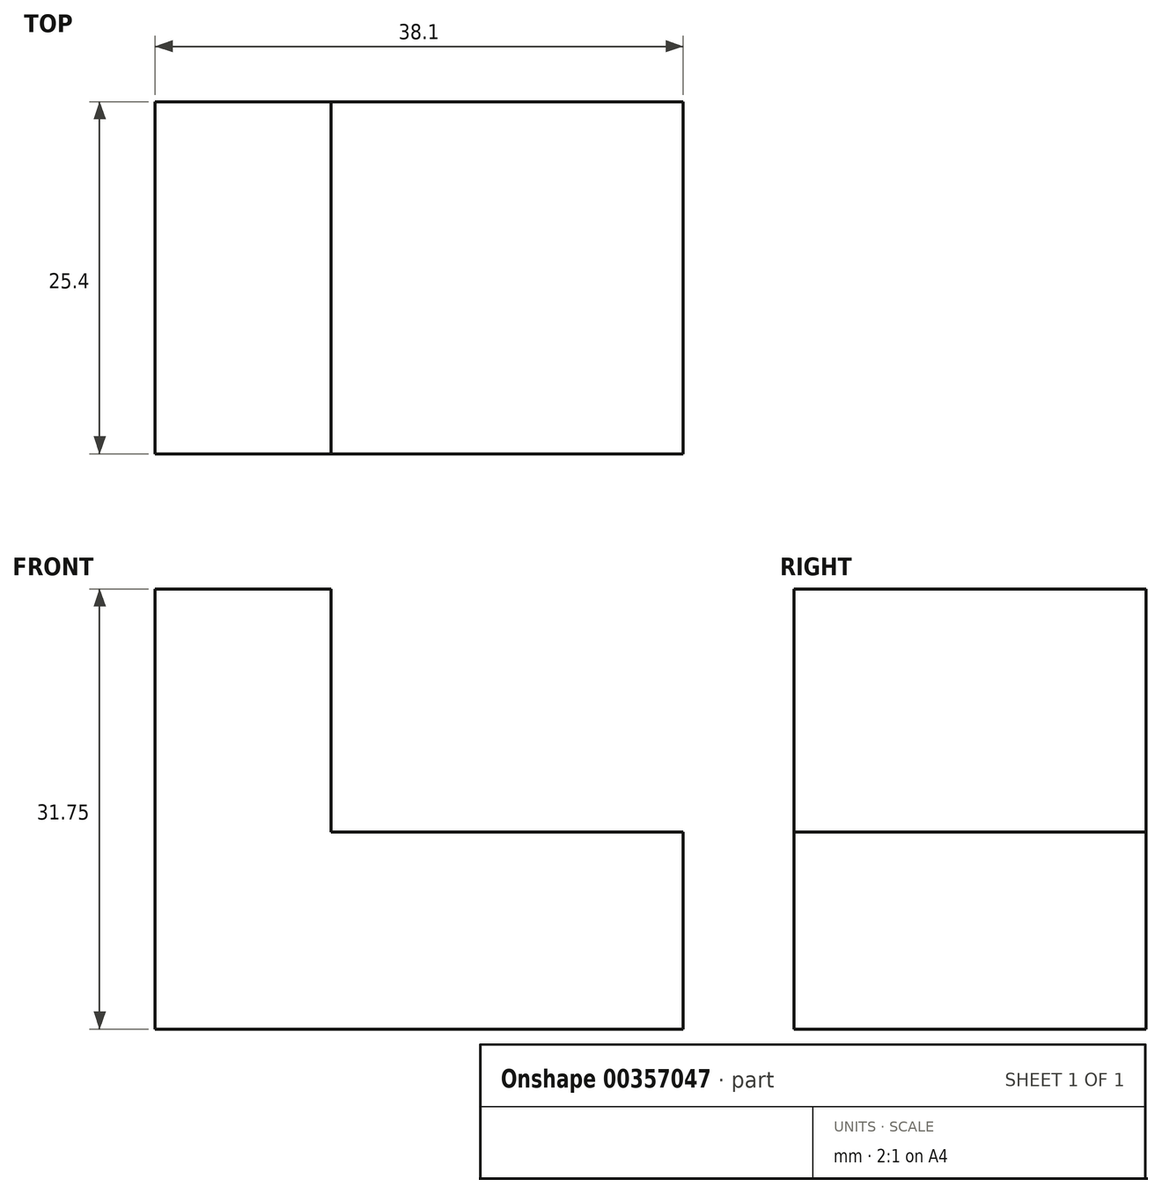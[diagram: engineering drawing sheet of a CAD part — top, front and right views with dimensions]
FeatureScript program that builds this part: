
annotation { "Feature Type Name" : "Feature", "Feature Type Description" : "" }
export const myFeature = defineFeature(function(context is Context, id is Id, definition is map)
    precondition{}
    {
        {
            var Q0;
            Q0=qCreatedBy(makeId("Front.planeOp"),FACE);
            var sketch = newSketch(context, id + "F0", { "sketchPlane" : qUnion([Q0])});
            skLineSegment(sketch, "E0", {"start": v(0, 0) * mm, "end": v(38.1, 0) * mm});
            skLineSegment(sketch, "E1", {"start": v(38.1, 0) * mm, "end": v(38.1, 14.22) * mm});
            skLineSegment(sketch, "E2", {"start": v(38.1, 14.22) * mm, "end": v(12.7, 14.22) * mm});
            skLineSegment(sketch, "E3", {"start": v(12.7, 14.22) * mm, "end": v(12.7, 31.75) * mm});
            skLineSegment(sketch, "E4", {"start": v(12.7, 31.75) * mm, "end": v(0, 31.75) * mm});
            skLineSegment(sketch, "E5", {"start": v(0, 31.75) * mm, "end": v(0, 0) * mm});
            skSolve(sketch);
        }
        {
            var Q0;
            Q0 = qSketchRegion(id + "F0", true);
            extrude(context, id + "F1", {"entities" : qUnion([Q0]), "depth" : 25.4 * mm});
        }
    });
